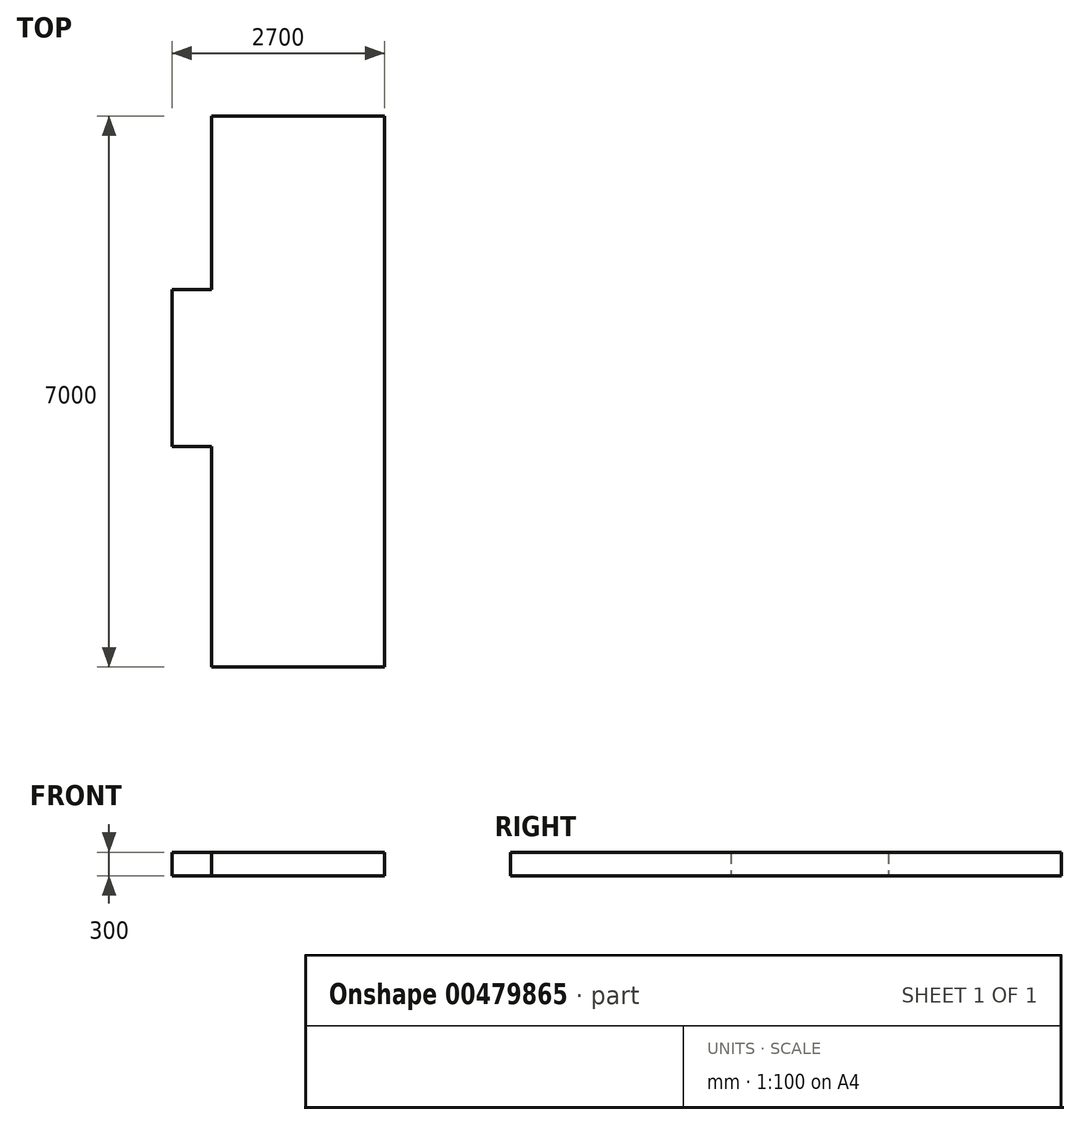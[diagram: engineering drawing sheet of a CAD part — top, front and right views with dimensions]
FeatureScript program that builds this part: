
annotation { "Feature Type Name" : "Feature", "Feature Type Description" : "" }
export const myFeature = defineFeature(function(context is Context, id is Id, definition is map)
    precondition{}
    {
        {
            var Q0;
            Q0=qCreatedBy(makeId("Top.planeOp"),FACE);
            var sketch = newSketch(context, id + "F0", { "sketchPlane" : qUnion([Q0])});
            skLineSegment(sketch, "E0", {"start": v(0, 0) * mm, "end": v(0, -2200) * mm});
            skLineSegment(sketch, "E1", {"start": v(0, -2200) * mm, "end": v(-500, -2200) * mm});
            skLineSegment(sketch, "E2", {"start": v(-500, -2200) * mm, "end": v(-500, -4200) * mm});
            skLineSegment(sketch, "E3", {"start": v(-500, -4200) * mm, "end": v(0, -4200) * mm});
            skLineSegment(sketch, "E4", {"start": v(0, -4200) * mm, "end": v(0, -7000) * mm});
            skLineSegment(sketch, "E5", {"start": v(0, -7000) * mm, "end": v(2200, -7000) * mm});
            skLineSegment(sketch, "E6", {"start": v(2200, -7000) * mm, "end": v(2200, 0) * mm});
            skLineSegment(sketch, "E7", {"start": v(2200, 0) * mm, "end": v(0, 0) * mm});
            skSolve(sketch);
        }
        {
            var Q0;
            Q0 = qSketchRegion(id + "F0", true);
            extrude(context, id + "F1", {"entities" : qUnion([Q0]), "depth" : 300 * mm});
        }
    });
